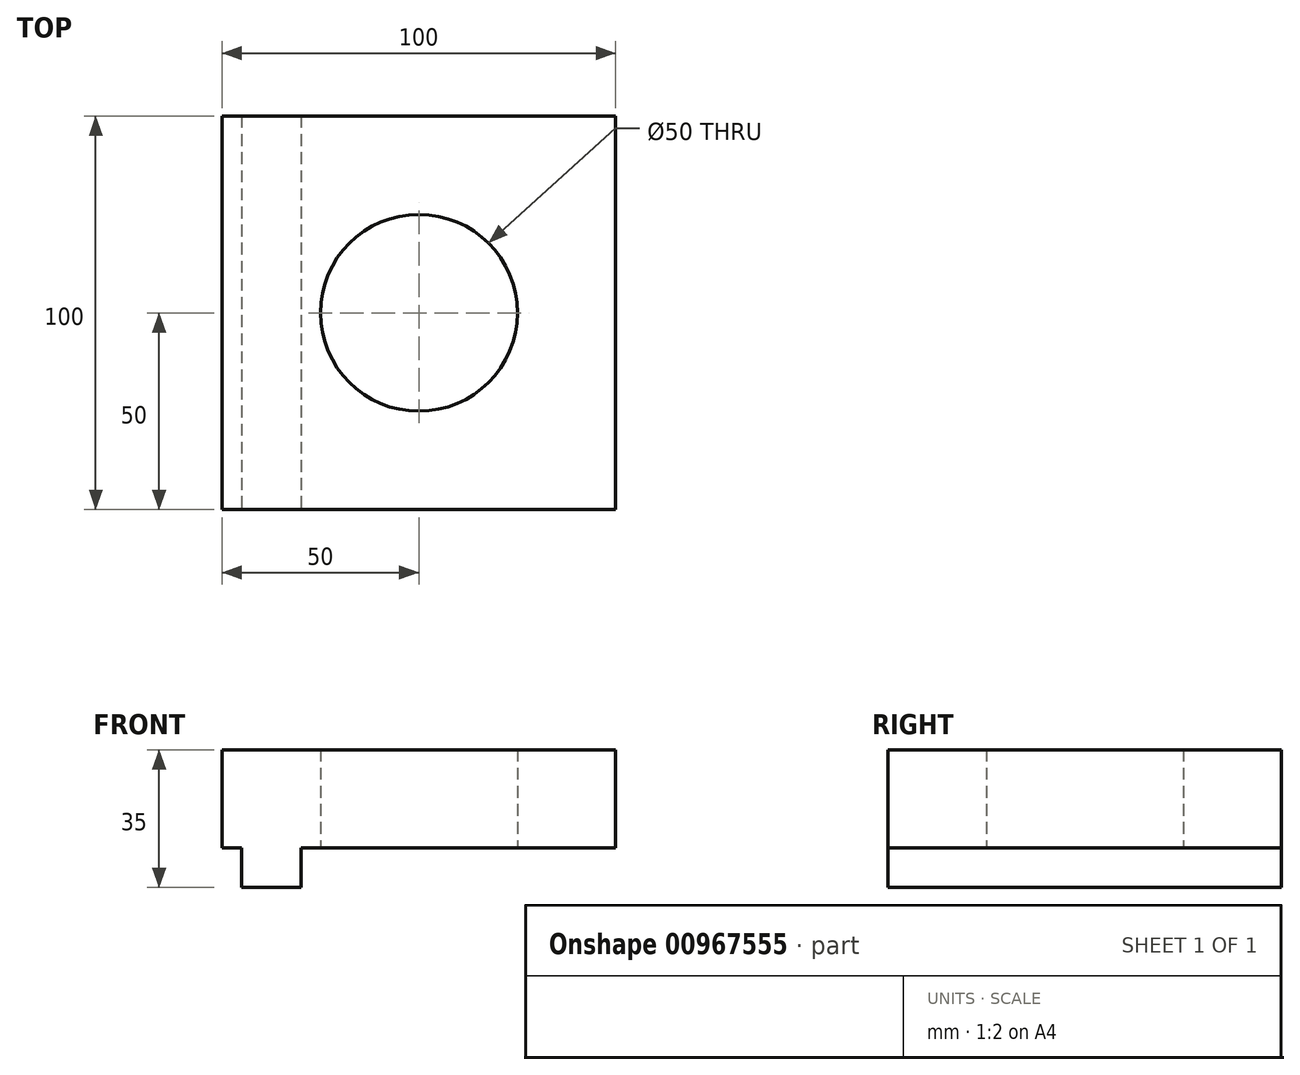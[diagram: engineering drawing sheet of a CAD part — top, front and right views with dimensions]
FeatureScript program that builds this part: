
annotation { "Feature Type Name" : "Feature", "Feature Type Description" : "" }
export const myFeature = defineFeature(function(context is Context, id is Id, definition is map)
    precondition{}
    {
        {
            var Q0;
            Q0=qCreatedBy(makeId("Top.planeOp"),FACE);
            var sketch = newSketch(context, id + "F0", { "sketchPlane" : qUnion([Q0])});
            skLineSegment(sketch, "E0.bottom", {"start": v(-50, 50) * mm, "end": v(50, 50) * mm});
            skLineSegment(sketch, "E0.top", {"start": v(-50, -50) * mm, "end": v(50, -50) * mm});
            skLineSegment(sketch, "E0.left", {"start": v(-50, 50) * mm, "end": v(-50, -50) * mm});
            skLineSegment(sketch, "E0.right", {"start": v(50, 50) * mm, "end": v(50, -50) * mm});
            skPoint(sketch, "E0.middle", {"position": v(0, 0) * mm});
            skCircle(sketch, "E1", {"center": v(0, 0) * mm, "radius": 25 * mm});
            skSolve(sketch);
        }
        {
            var Q0;
            Q0=makeQuery(id+"F0.imprint","IMPRINT",FACE,{"disambiguationData":[TD([[makeQuery(id+"F0.imprint","IMPRINT",EDGE,{"derivedFrom":sQuery(id+"F0.wireOp",EDGE,"E0.bottom")}),-1.0]])]});
            var sketch = newSketch(context, id + "F1", { "sketchPlane" : qUnion([Q0])});
            skLineSegment(sketch, "E2.bottom", {"start": v(-45, 50) * mm, "end": v(-30, 50) * mm});
            skLineSegment(sketch, "E2.top", {"start": v(-45, -50) * mm, "end": v(-30, -50) * mm});
            skLineSegment(sketch, "E2.left", {"start": v(-45, 50) * mm, "end": v(-45, -50) * mm});
            skLineSegment(sketch, "E2.right", {"start": v(-30, 50) * mm, "end": v(-30, -50) * mm});
            skPoint(sketch, "E2.middle", {"position": v(-37.5, 0) * mm});
            skSolve(sketch);
        }
        {
            var Q0;
            Q0=makeQuery(id+"F0.imprint","IMPRINT",FACE,{"disambiguationData":[TD([[makeQuery(id+"F0.imprint","IMPRINT",EDGE,{"derivedFrom":sQuery(id+"F0.wireOp",EDGE,"E0.bottom")}),-1.0]])]});
            var Q1;
            Q1=sQuery(id+"F0.wireOp",EDGE,"E1");
            var Q2;
            Q2 = qBodyType(qCreatedBy(id + "F0" ,EDGE), BodyType.WIRE);
            extrude(context, id + "F2", {"entities" : qUnion([Q0]), "surfaceEntities" : qUnion([Q1, Q2]), "depth" : 25 * mm, "offsetDistance" : 25 * mm});
        }
        {
            var Q0;
            Q0=makeQuery(id+"F1.imprint","IMPRINT",FACE,{"disambiguationData":[TD([[makeQuery(id+"F1.imprint","IMPRINT",EDGE,{"derivedFrom":sQuery(id+"F1.wireOp",EDGE,"E2.bottom")}),-1.0]])]});
            extrude(context, id + "F3", {"entities" : qUnion([Q0]), "operationType" : NewBodyOperationType.ADD, "oppositeDirection" : true, "depth" : 10 * mm, "offsetDistance" : 25 * mm});
        }
    });
